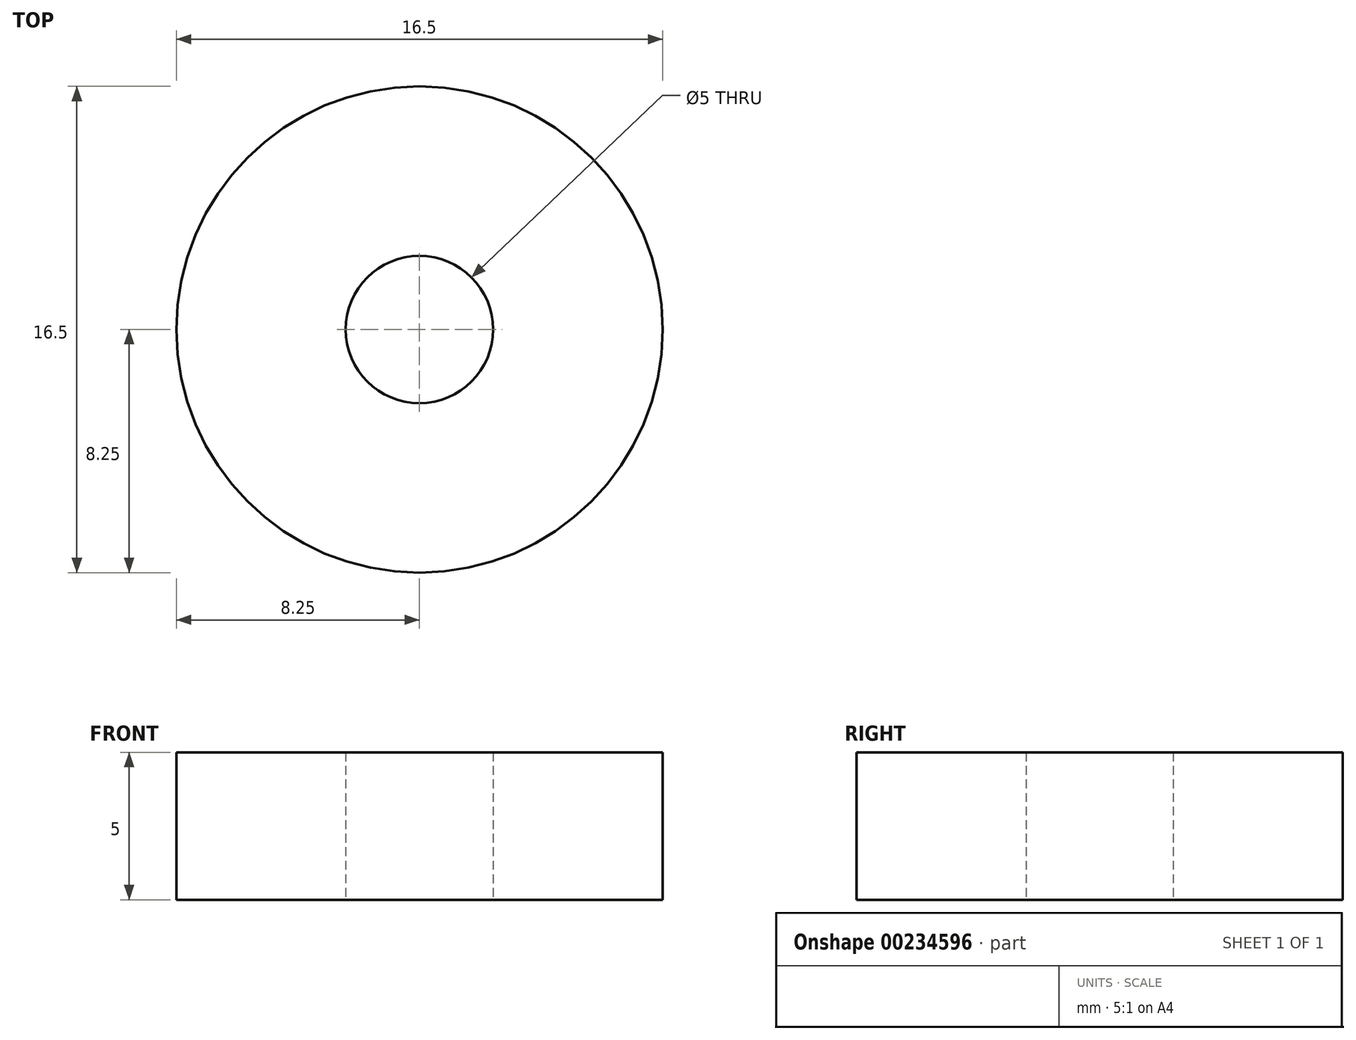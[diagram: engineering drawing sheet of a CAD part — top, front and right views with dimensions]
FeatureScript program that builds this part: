
annotation { "Feature Type Name" : "Feature", "Feature Type Description" : "" }
export const myFeature = defineFeature(function(context is Context, id is Id, definition is map)
    precondition{}
    {
        {
            var Q0;
            Q0=qCreatedBy(makeId("Top.planeOp"),FACE);
            var sketch = newSketch(context, id + "F0", { "sketchPlane" : qUnion([Q0])});
            skCircle(sketch, "E0", {"center": v(0, 0) * mm, "radius": 2.5 * mm});
            skCircle(sketch, "E1", {"center": v(0, 0) * mm, "radius": 8.25 * mm});
            skSolve(sketch);
        }
        {
            var Q0;
            Q0=makeQuery(id+"F0.imprint","IMPRINT",FACE,{"disambiguationData":[TD([[makeQuery(id+"F0.imprint","IMPRINT",EDGE,{"derivedFrom":sQuery(id+"F0.wireOp",EDGE,"E0")}),-1.0]])]});
            extrude(context, id + "F1", {"entities" : qUnion([Q0]), "depth" : 5 * mm});
        }
    });
